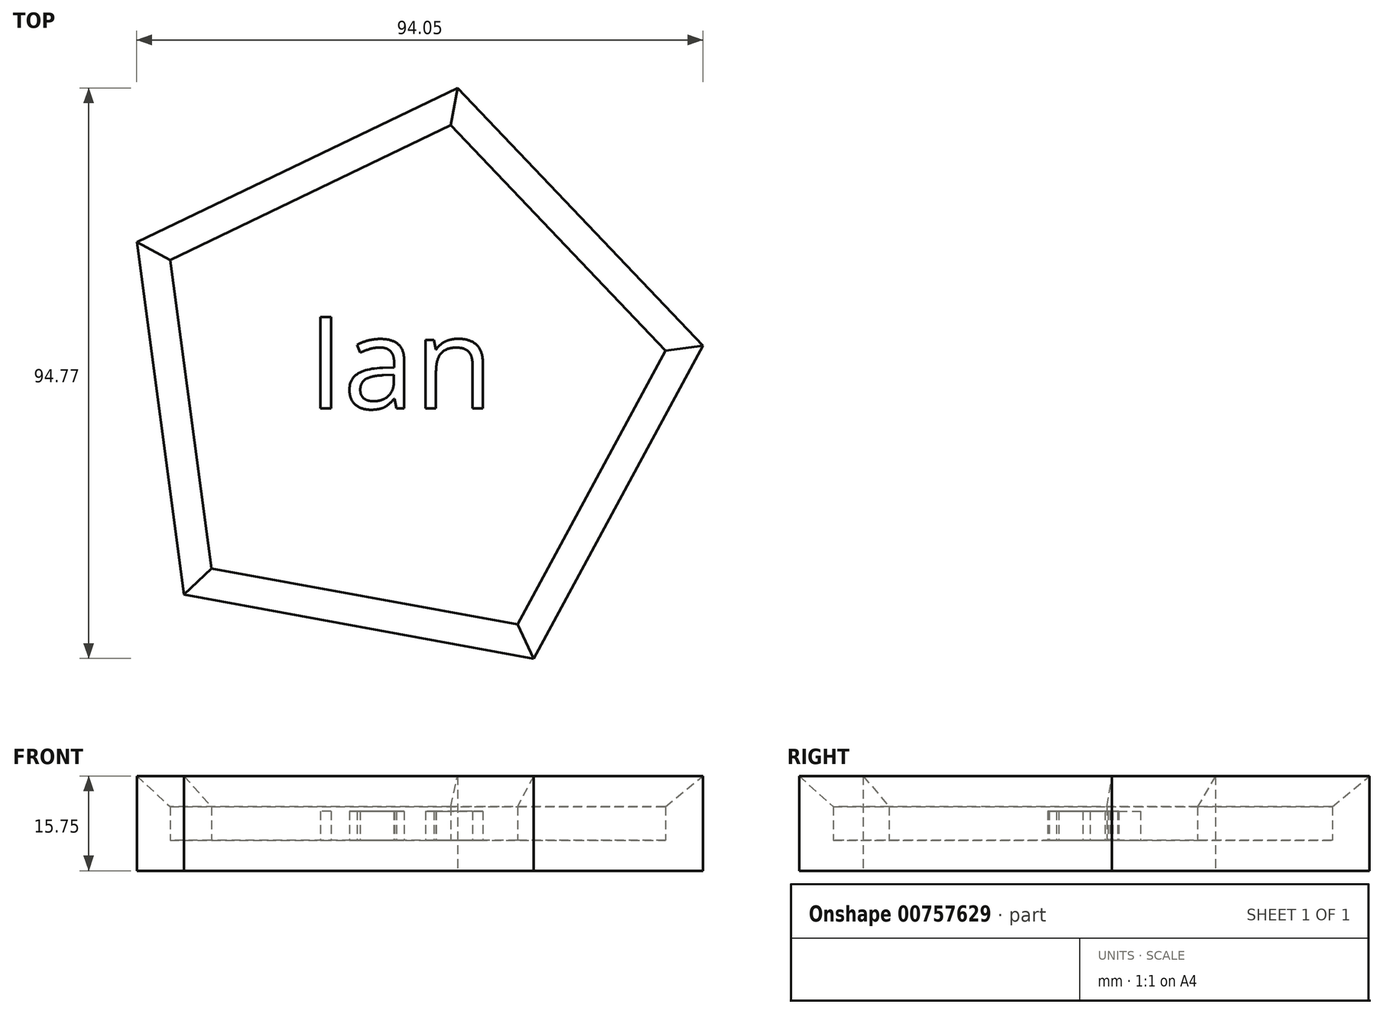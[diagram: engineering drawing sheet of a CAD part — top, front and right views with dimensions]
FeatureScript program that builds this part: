
annotation { "Feature Type Name" : "Feature", "Feature Type Description" : "" }
export const myFeature = defineFeature(function(context is Context, id is Id, definition is map)
    precondition{}
    {
        {
            var Q0;
            Q0=qCreatedBy(makeId("Top.planeOp"),FACE);
            var sketch = newSketch(context, id + "F0", { "sketchPlane" : qUnion([Q0])});
            skCircle(sketch, "E0.cCircle", {"center": v(0, 0) * mm, "radius": 40.67 * mm, "construction": true});
            skLineSegment(sketch, "E0.0", {"start": v(49.82, 6.67) * mm, "end": v(21.74, -45.32) * mm});
            skLineSegment(sketch, "E0.1", {"start": v(21.74, -45.32) * mm, "end": v(-36.39, -34.68) * mm});
            skLineSegment(sketch, "E0.2", {"start": v(-36.39, -34.68) * mm, "end": v(-44.23, 23.89) * mm});
            skLineSegment(sketch, "E0.3", {"start": v(-44.23, 23.89) * mm, "end": v(9.05, 49.45) * mm});
            skLineSegment(sketch, "E0.4", {"start": v(9.05, 49.45) * mm, "end": v(49.82, 6.67) * mm});
            skPoint(sketch, "E0.0.midPoint", {"position": v(35.78, -19.33) * mm});
            skSolve(sketch);
        }
        {
            var Q0;
            Q0=makeQuery(id+"F0.imprint","IMPRINT",FACE,{"disambiguationData":[TD([[makeQuery(id+"F0.imprint","IMPRINT",EDGE,{"derivedFrom":sQuery(id+"F0.wireOp",EDGE,"E0.0")}),-1.0]])]});
            extrude(context, id + "F1", {"entities" : qUnion([Q0]), "depth" : 15.75 * mm, "offsetDistance" : 25.4 * mm});
        }
        {
            var Q0;
            Q0=makeQuery(id+"F1.opExtrude","CAP_FACE",FACE,{"disambiguationData":[OSD([sQuery(id+"F0.wireOp",EDGE,"E0.0"),sQuery(id+"F0.wireOp",EDGE,"E0.1"),sQuery(id+"F0.wireOp",EDGE,"E0.2"),sQuery(id+"F0.wireOp",EDGE,"E0.3"),sQuery(id+"F0.wireOp",EDGE,"E0.4")])],"isStart":false});
            shell(context, id + "F2", {"entities" : qUnion([Q0]), "thickness" : 5.08 * mm});
        }
        {
            var Q0;
            {var subQ0=sQuery(id+"F0.wireOp",EDGE,"E0.4");Q0=makeQuery(id+"F2.opShell","OFFSET_EDGE",EDGE,{"disambiguationData":[OSD([subQ0]),TDD([makeQuery(id+"F1.opExtrude","CAP_EDGE",EDGE,{"disambiguationData":[OSD([subQ0])],"isStart":false})])]});}
            var Q1;
            {var subQ0=sQuery(id+"F0.wireOp",EDGE,"E0.2");Q1=makeQuery(id+"F2.opShell","OFFSET_EDGE",EDGE,{"disambiguationData":[OSD([subQ0]),TDD([makeQuery(id+"F1.opExtrude","CAP_EDGE",EDGE,{"disambiguationData":[OSD([subQ0])],"isStart":false})])]});}
            var Q2;
            {var subQ0=sQuery(id+"F0.wireOp",EDGE,"E0.3");Q2=makeQuery(id+"F2.opShell","OFFSET_EDGE",EDGE,{"disambiguationData":[OSD([subQ0]),TDD([makeQuery(id+"F1.opExtrude","CAP_EDGE",EDGE,{"disambiguationData":[OSD([subQ0])],"isStart":false})])]});}
            var Q3;
            {var subQ0=sQuery(id+"F0.wireOp",EDGE,"E0.1");Q3=makeQuery(id+"F2.opShell","OFFSET_EDGE",EDGE,{"disambiguationData":[OSD([subQ0]),TDD([makeQuery(id+"F1.opExtrude","CAP_EDGE",EDGE,{"disambiguationData":[OSD([subQ0])],"isStart":false})])]});}
            var Q4;
            {var subQ0=sQuery(id+"F0.wireOp",EDGE,"E0.0");Q4=makeQuery(id+"F2.opShell","OFFSET_EDGE",EDGE,{"disambiguationData":[OSD([subQ0]),TDD([makeQuery(id+"F1.opExtrude","CAP_EDGE",EDGE,{"disambiguationData":[OSD([subQ0])],"isStart":false})])]});}
            chamfer(context, id + "F3", {"entities" : qUnion([Q0, Q1, Q2, Q3, Q4]), "width" : 5.08 * mm, "tangentPropagation" : true});
        }
        {
            var Q0;
            Q0=makeQuery(id+"F2.opShell","OFFSET_FACE",FACE,{"disambiguationData":[OSD([sQuery(id+"F0.wireOp",EDGE,"E0.0"),sQuery(id+"F0.wireOp",EDGE,"E0.1"),sQuery(id+"F0.wireOp",EDGE,"E0.2"),sQuery(id+"F0.wireOp",EDGE,"E0.3"),sQuery(id+"F0.wireOp",EDGE,"E0.4")])]});
            var sketch = newSketch(context, id + "F4", { "sketchPlane" : qUnion([Q0])});
            skText(sketch, "E1", { "text": "Ian\n", "fontName": "OpenSans-Regular.ttf"});
            const initialGuessF4  = {"E1": [-0.0158, -0.00378, 1, 0, 0.0153]};
            skSetInitialGuess(sketch, initialGuessF4);
            skSolve(sketch);
        }
        {
            var Q0;
            Q0 = qSketchRegion(id + "F4", true);
            extrude(context, id + "F5", {"entities" : qUnion([Q0]), "operationType" : NewBodyOperationType.ADD, "depth" : 4.83 * mm, "offsetDistance" : 25.4 * mm});
        }
    });
